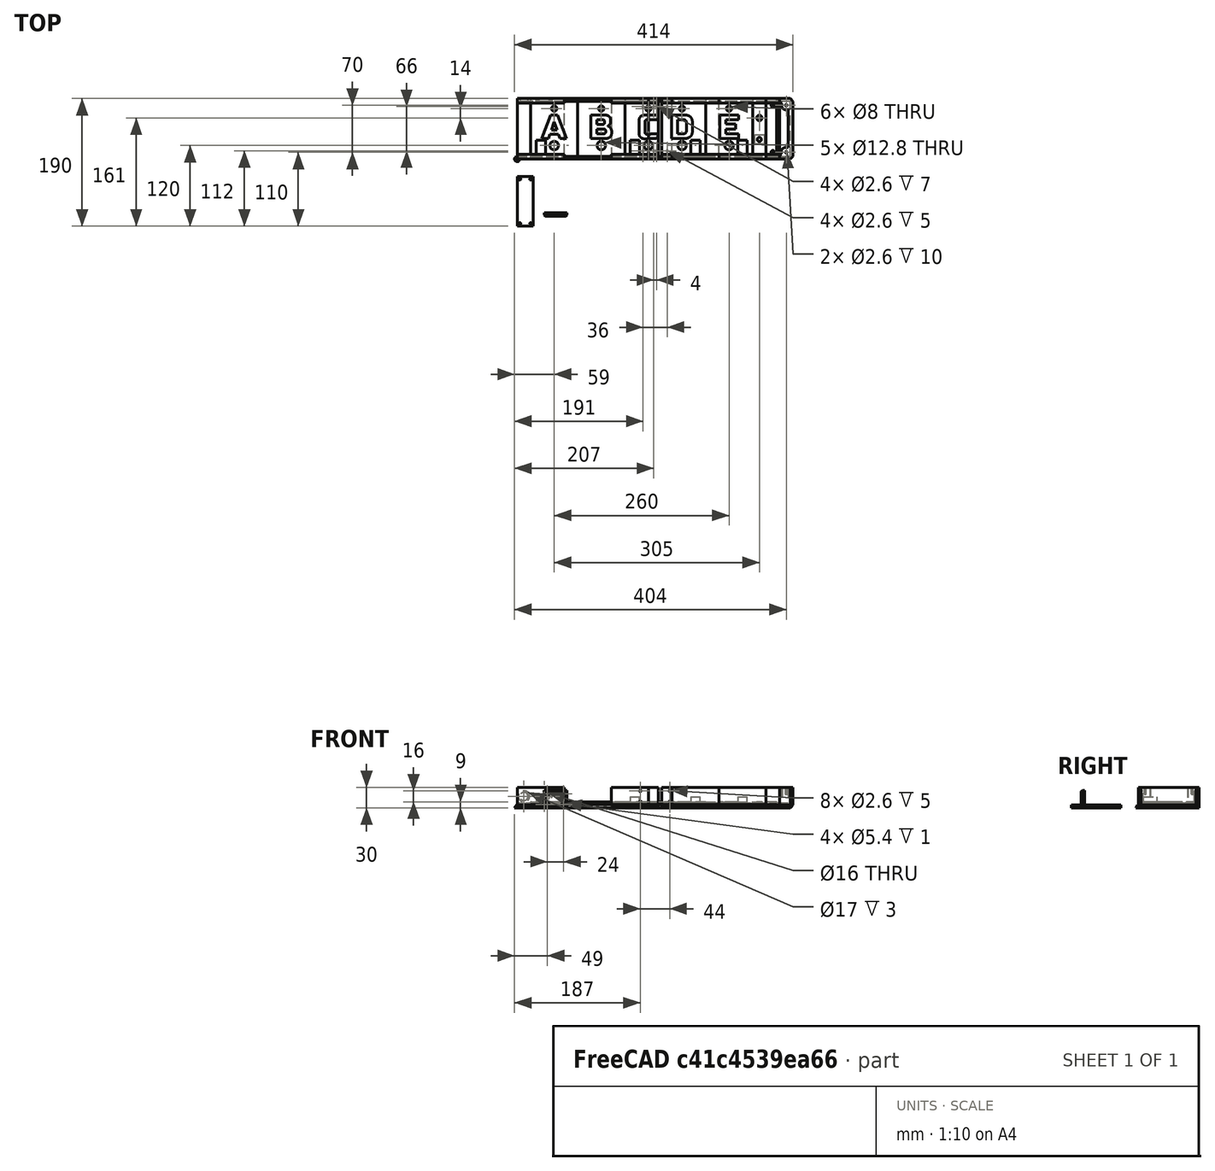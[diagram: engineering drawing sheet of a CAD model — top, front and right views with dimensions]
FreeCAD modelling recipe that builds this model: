
FCSTD DOCUMENT  (FreeCAD 1.0R39319 (Git))
Label: controller
License: All rights reserved
LicenseURL: https://en.wikipedia.org/wiki/All_rights_reserved
objects: Sketcher::SketchObject×34, PartDesign::Body×24, PartDesign::Pocket×17, PartDesign::Pad×15, PartDesign::FeatureBase×15, PartDesign::Chamfer×8, Part::FeaturePython×7, Part::Part2DObjectPython×5, Part::Extrusion×5, Part::Cut×5, App::Part×4, App::Link×4, Part::Plane×2, App::DocumentObjectGroup×2, PartDesign::Plane×1, PartDesign::AdditiveLoft×1, App::FeaturePython×1, Assembly::JointGroup×1, Assembly::AssemblyObject×1
note: 270 computed .brp shape members not serialized (recipe doc carries the construction recipe); baked Part::Feature solids carry a one-line shape summary decoded from their .brp

FEATURE [Sketcher::SketchObject] Sketch
  ArcFitTolerance = 1e-06
  AttachmentSupport = -> [XY_Plane]
  FullyConstrained = true
  MakeInternals = false
  MapMode = 5
  sketch-geometry (4):
    g0: LineSegment StartX=0 StartY=0 StartZ=0 EndX=70 EndY=0 EndZ=0
    g1: LineSegment StartX=70 StartY=0 StartZ=0 EndX=70 EndY=90 EndZ=0
    g2: LineSegment StartX=70 StartY=90 StartZ=0 EndX=0 EndY=90 EndZ=0
    g3: LineSegment StartX=0 StartY=90 StartZ=0 EndX=0 EndY=0 EndZ=0
  constraints (11):
    c: Coincident(g0,g1)
    c: Coincident(g1,g2)
    c: Coincident(g2,g3)
    c: Coincident(g3,g0)
    c: Horizontal(g0)
    c: Horizontal(g2)
    c: Vertical(g1)
    c: Vertical(g3)
    c: Distance(g1,g3) = 70
    c: Distance(g0,g2) = 90
    c: Coincident(g0,g-1)
FEATURE [PartDesign::Pad] Pad
  Direction = (0,0,1)
  Length = 7
  Length2 = 10
  Profile = -> Sketch
  ReferenceAxis = -> Sketch [N_Axis]
  Refine = true
  Suppressed = false
  Type = 0
FEATURE [Sketcher::SketchObject] Sketch001
  ArcFitTolerance = 1e-06
  AttachmentSupport = -> [Pad]
  ExternalGeometry = -> [Pad]
  FullyConstrained = true
  MakeInternals = false
  MapMode = 5
  Placement = pos=(0,0,7) rot=(0,0,1;0rad)
  sketch-geometry (4):
    g0: LineSegment StartX=0 StartY=90 StartZ=0 EndX=0 EndY=83 EndZ=0
    g1: LineSegment StartX=0 StartY=83 StartZ=0 EndX=70 EndY=83 EndZ=0
    g2: LineSegment StartX=70 StartY=83 StartZ=0 EndX=70 EndY=90 EndZ=0
    g3: LineSegment StartX=70 StartY=90 StartZ=0 EndX=0 EndY=90 EndZ=0
  constraints (11):
    c: Coincident(g0,g1)
    c: Coincident(g1,g2)
    c: Coincident(g2,g3)
    c: Coincident(g3,g0)
    c: Vertical(g0)
    c: Vertical(g2)
    c: Horizontal(g1)
    c: Horizontal(g3)
    c: Distance(g0,g2) = 70
    c: Distance(g1,g3) = 7
    c: Coincident(g0,g-3)
FEATURE [PartDesign::Pad] Pad001
  BaseFeature = -> Pad
  Direction = (0,0,1)
  Length = 23
  Length2 = 10
  Profile = -> Sketch001
  ReferenceAxis = -> Sketch001 [N_Axis]
  Refine = true
  Suppressed = false
  Type = 0
FEATURE [Sketcher::SketchObject] Sketch002
  ArcFitTolerance = 1e-06
  AttachmentSupport = -> [Pad001]
  ExternalGeometry = -> [Pad001]
  FullyConstrained = true
  MakeInternals = false
  MapMode = 5
  Placement = pos=(0,0,7) rot=(0,0,1;0rad)
  sketch-geometry (4):
    g0: LineSegment StartX=28 StartY=0 StartZ=0 EndX=42 EndY=0 EndZ=0
    g1: LineSegment StartX=42 StartY=0 StartZ=0 EndX=42 EndY=28 EndZ=0
    g2: LineSegment StartX=42 StartY=28 StartZ=0 EndX=28 EndY=28 EndZ=0
    g3: LineSegment StartX=28 StartY=28 StartZ=0 EndX=28 EndY=0 EndZ=0
  constraints (12):
    c: Coincident(g0,g1)
    c: Coincident(g1,g2)
    c: Coincident(g2,g3)
    c: Coincident(g3,g0)
    c: Horizontal(g0)
    c: Horizontal(g2)
    c: Vertical(g1)
    c: Vertical(g3)
    c: Distance(g1,g3) = 14
    c: Distance(g0,g2) = 28
    c: PointOnObject(g0,g-1)
    c: Distance(g-3,g1) = 28
FEATURE [PartDesign::Pad] Pad002
  BaseFeature = -> Pad001
  Direction = (0,0,1)
  Length = 9
  Length2 = 10
  Profile = -> Sketch002
  ReferenceAxis = -> Sketch002 [N_Axis]
  Refine = true
  Suppressed = false
  Type = 0
FEATURE [Sketcher::SketchObject] Sketch003
  ArcFitTolerance = 1e-06
  AttachmentSupport = -> [Pad002]
  FullyConstrained = true
  MakeInternals = false
  MapMode = 5
  Placement = pos=(0,0,7) rot=(0,0,1;0rad)
  sketch-geometry (4):
    g0: LineSegment StartX=0 StartY=0 StartZ=0 EndX=70 EndY=0 EndZ=0
    g1: LineSegment StartX=70 StartY=0 StartZ=0 EndX=70 EndY=7 EndZ=0
    g2: LineSegment StartX=70 StartY=7 StartZ=0 EndX=0 EndY=7 EndZ=0
    g3: LineSegment StartX=0 StartY=7 StartZ=0 EndX=0 EndY=0 EndZ=0
  constraints (11):
    c: Coincident(g0,g1)
    c: Coincident(g1,g2)
    c: Coincident(g2,g3)
    c: Coincident(g3,g0)
    c: Horizontal(g0)
    c: Horizontal(g2)
    c: Vertical(g1)
    c: Vertical(g3)
    c: Distance(g1,g3) = 70
    c: Distance(g0,g2) = 7
    c: Coincident(g0,g-1)
FEATURE [PartDesign::Pad] Pad003
  BaseFeature = -> Pad002
  Direction = (0,0,1)
  Length = 23
  Length2 = 10
  Profile = -> Sketch003
  ReferenceAxis = -> Sketch003 [N_Axis]
  Refine = true
  Suppressed = false
  Type = 0
FEATURE [Part::Plane] Plane
  AttacherType = Attacher::AttachEngine3D
  Length = 100
  Placement = pos=(195,0,0) rot=(0.58,0.58,0.58;2.0944rad)
  Width = 100
FEATURE [Sketcher::SketchObject] Sketch010
  ArcFitTolerance = 1e-06
  AttachmentSupport = -> [XY_Plane005]
  FullyConstrained = true
  MakeInternals = false
  MapMode = 5
  sketch-geometry (4):
    g0: LineSegment StartX=0 StartY=0 StartZ=0 EndX=20 EndY=0 EndZ=0
    g1: LineSegment StartX=20 StartY=0 StartZ=0 EndX=20 EndY=90 EndZ=0
    g2: LineSegment StartX=20 StartY=90 StartZ=0 EndX=0 EndY=90 EndZ=0
    g3: LineSegment StartX=0 StartY=90 StartZ=0 EndX=0 EndY=0 EndZ=0
  constraints (11):
    c: Coincident(g0,g1)
    c: Coincident(g1,g2)
    c: Coincident(g2,g3)
    c: Coincident(g3,g0)
    c: Horizontal(g0)
    c: Horizontal(g2)
    c: Vertical(g1)
    c: Vertical(g3)
    c: Distance(g1,g3) = 20
    c: Distance(g0,g2) = 90
    c: Coincident(g0,g-1)
FEATURE [PartDesign::Pad] Pad004
  Direction = (0,0,1)
  Length = 7
  Length2 = 10
  Profile = -> Sketch010
  ReferenceAxis = -> Sketch010 [N_Axis]
  Refine = true
  Suppressed = false
  Type = 0
FEATURE [Sketcher::SketchObject] Sketch011
  ArcFitTolerance = 1e-06
  AttachmentSupport = -> [Pad004]
  ExternalGeometry = -> [Pad004]
  FullyConstrained = true
  MakeInternals = false
  MapMode = 5
  Placement = pos=(0,0,7) rot=(0,0,1;0rad)
  sketch-geometry (8):
    g0: LineSegment StartX=20 StartY=90 StartZ=0 EndX=7 EndY=90 EndZ=0
    g1: LineSegment StartX=7 StartY=90 StartZ=0 EndX=7 EndY=83 EndZ=0
    g2: LineSegment StartX=7 StartY=83 StartZ=0 EndX=20 EndY=83 EndZ=0
    g3: LineSegment StartX=20 StartY=83 StartZ=0 EndX=20 EndY=90 EndZ=0
    g4: LineSegment StartX=20 StartY=0 StartZ=0 EndX=20 EndY=7 EndZ=0
    g5: LineSegment StartX=20 StartY=7 StartZ=0 EndX=7 EndY=7 EndZ=0
    g6: LineSegment StartX=7 StartY=7 StartZ=0 EndX=7 EndY=0 EndZ=0
    g7: LineSegment StartX=7 StartY=0 StartZ=0 EndX=20 EndY=0 EndZ=0
  constraints (22):
    c: Coincident(g0,g1)
    c: Coincident(g1,g2)
    c: Coincident(g2,g3)
    c: Coincident(g3,g0)
    c: Horizontal(g0)
    c: Horizontal(g2)
    c: Vertical(g1)
    c: Vertical(g3)
    c: Distance(g1,g3) = 13
    c: Distance(g0,g2) = 7
    c: Coincident(g0,g-4)
    c: Coincident(g4,g5)
    c: Coincident(g5,g6)
    c: Coincident(g6,g7)
    c: Coincident(g7,g4)
    c: Vertical(g4)
    c: Vertical(g6)
    c: Horizontal(g5)
    c: Horizontal(g7)
    c: Distance(g4,g6) = 13
    c: Distance(g5,g7) = 7
    c: Coincident(g4,g-4)
FEATURE [PartDesign::Pad] Pad005
  BaseFeature = -> Pad004
  Direction = (0,0,1)
  Length = 23
  Length2 = 10
  Profile = -> Sketch011
  ReferenceAxis = -> Sketch011 [N_Axis]
  Refine = true
  Suppressed = false
  Type = 0
FEATURE [Sketcher::SketchObject] Sketch012
  ArcFitTolerance = 1e-06
  AttachmentSupport = -> [Pad005]
  FullyConstrained = true
  MakeInternals = false
  MapMode = 5
  Placement = pos=(0,0,7) rot=(0,0,1;0rad)
  sketch-geometry (4):
    g0: LineSegment StartX=0 StartY=0 StartZ=0 EndX=7 EndY=0 EndZ=0
    g1: LineSegment StartX=7 StartY=0 StartZ=0 EndX=7 EndY=90 EndZ=0
    g2: LineSegment StartX=7 StartY=90 StartZ=0 EndX=0 EndY=90 EndZ=0
    g3: LineSegment StartX=0 StartY=90 StartZ=0 EndX=0 EndY=0 EndZ=0
  constraints (11):
    c: Coincident(g0,g1)
    c: Coincident(g1,g2)
    c: Coincident(g2,g3)
    c: Coincident(g3,g0)
    c: Horizontal(g0)
    c: Horizontal(g2)
    c: Vertical(g1)
    c: Vertical(g3)
    c: Distance(g1,g3) = 7
    c: Distance(g0,g2) = 90
    c: Coincident(g0,g-1)
FEATURE [PartDesign::Pad] Pad006
  BaseFeature = -> Pad005
  Direction = (0,0,1)
  Length = 23
  Length2 = 10
  Profile = -> Sketch012
  ReferenceAxis = -> Sketch012 [N_Axis]
  Refine = true
  Suppressed = false
  Type = 0
FEATURE [Sketcher::SketchObject] Sketch013
  ArcFitTolerance = 1e-06
  AttachmentSupport = -> [Pad006]
  ExternalGeometry = -> [Pad006]
  FullyConstrained = true
  MakeInternals = false
  MapMode = 5
  Placement = pos=(0,0,7) rot=(0,0,1;0rad)
  sketch-geometry (2):
    g0: Circle CenterX=10 CenterY=80 CenterZ=0 NormalX=0 NormalY=0 NormalZ=1 AngleXU=0 Radius=7.5
    g1: Circle CenterX=10 CenterY=10 CenterZ=0 NormalX=0 NormalY=0 NormalZ=1 AngleXU=0 Radius=7
  constraints (6):
    c: Diameter(g0) = 15
    c: DistanceY(g0,g-3) = 10
    c: DistanceX(g-3,g0) = 10
    c: Diameter(g1) = 14
    c: DistanceX(g-1,g1) = 10
    c: DistanceY(g-1,g1) = 10
FEATURE [PartDesign::Pad] Pad007
  BaseFeature = -> Pad006
  Direction = (0,0,1)
  Length = 23
  Length2 = 10
  Profile = -> Sketch013
  ReferenceAxis = -> Sketch013 [N_Axis]
  Refine = true
  Suppressed = false
  Type = 0
FEATURE [Sketcher::SketchObject] Sketch014
  ArcFitTolerance = 1e-06
  AttachmentSupport = -> [Pad007]
  ExternalGeometry = -> [Pad007]
  FullyConstrained = true
  MakeInternals = false
  MapMode = 5
  Placement = pos=(0,0,30) rot=(0,0,1;0rad)
  sketch-geometry (2):
    g0: Circle CenterX=10 CenterY=80 CenterZ=0 NormalX=0 NormalY=0 NormalZ=1 AngleXU=0 Radius=1.3
    g1: Circle CenterX=10 CenterY=10 CenterZ=0 NormalX=0 NormalY=0 NormalZ=1 AngleXU=0 Radius=1.3
  constraints (6):
    c: Diameter(g0) = 2.6
    c: Diameter(g1) = 2.6
    c: DistanceY(g0,g-3) = 10
    c: DistanceX(g-3,g0) = 10
    c: DistanceX(g-1,g1) = 10
    c: DistanceY(g-1,g1) = 10
FEATURE [PartDesign::Pocket] Pocket
  BaseFeature = -> Pad007
  Direction = (0,0,-1)
  Length = 10
  Length2 = 5
  Profile = -> Sketch014
  ReferenceAxis = -> Sketch014 [N_Axis]
  Refine = true
  Suppressed = false
  Type = 0
FEATURE [PartDesign::Chamfer] Chamfer
  Angle = 45
  Base = -> Pad003 [Edge1,Edge3]
  BaseFeature = -> Pad003
  ChamferType = 0
  FlipDirection = false
  Refine = true
  Size = 4
  Size2 = 1
  SupportTransform = false
  Suppressed = false
  UseAllEdges = false
FEATURE [PartDesign::Body] Body  label="base-module"
  AllowCompound = false
  Group = -> [Sketch,Pad,Sketch001,Pad001,Sketch002,Pad002,Sketch003,Pad003,Chamfer]
  Origin = -> Origin
  Placement = pos=(70,0,0) rot=(0,0,1;0rad)
  Tip = -> Chamfer
FEATURE [PartDesign::FeatureBase] Clone
  BaseFeature = -> Body
  Suppressed = false
FEATURE [PartDesign::FeatureBase] Clone001
  BaseFeature = -> Body
  Placement = pos=(70,0,0) rot=(0,0,1;0rad)
  Suppressed = false
FEATURE [PartDesign::Body] Body002  label="split-base-module"
  AllowCompound = false
  Group = -> [Clone001]
  Origin = -> Origin002
  Placement = pos=(70,0,0) rot=(0,0,1;0rad)
  Tip = -> Clone001
FEATURE [Part::FeaturePython] Slice  # WARN: FeaturePython — macro-defined, semantics opaque (R4)
  Base = -> Body002
  Mode = 1
  Tolerance = 0
  Tools = -> [Plane]
FEATURE [PartDesign::FeatureBase] Clone002
  BaseFeature = -> Body
  Placement = pos=(70,0,0) rot=(0,0,1;0rad)
  Suppressed = false
FEATURE [PartDesign::Body] Body003  label="base-module-clone"
  AllowCompound = false
  Group = -> [Clone002]
  Origin = -> Origin003
  Placement = pos=(160,0,0) rot=(0,0,1;0rad)
  Tip = -> Clone002
FEATURE [PartDesign::FeatureBase] Clone003
  BaseFeature = -> Body
  Placement = pos=(70,0,0) rot=(0,0,1;0rad)
  Suppressed = false
FEATURE [PartDesign::Body] Body004  label="base-module-clone001"
  AllowCompound = false
  Group = -> [Clone003]
  Origin = -> Origin004
  Placement = pos=(230,0,0) rot=(0,0,1;0rad)
  Tip = -> Clone003
FEATURE [PartDesign::Chamfer] Chamfer001
  Angle = 45
  Base = -> Pocket [Edge3,Edge4,Edge1]
  BaseFeature = -> Pocket
  ChamferType = 0
  FlipDirection = false
  Refine = true
  Size = 4
  Size2 = 1
  SupportTransform = false
  Suppressed = false
  UseAllEdges = false
FEATURE [PartDesign::FeatureBase] Clone004
  BaseFeature = -> Body
  Placement = pos=(70,0,0) rot=(0,0,1;0rad)
  Suppressed = false
FEATURE [Part::Plane] Plane001
  AttacherType = Attacher::AttachEngine3D
  Length = 200
  Placement = pos=(195,0,0) rot=(0.57735,0.57735,0.57735;2.0944rad)
  Width = 200
FEATURE [Sketcher::SketchObject] Sketch015
  ArcFitTolerance = 1e-06
  AttachmentSupport = -> [Clone004]
  ExternalGeometry = -> [Clone004]
  FullyConstrained = true
  MakeInternals = false
  MapMode = 5
  Placement = pos=(70,0,0) rot=(1,0,0;1.5708rad)
  sketch-geometry (4):
    g0: Circle CenterX=43 CenterY=25 CenterZ=0 NormalX=0 NormalY=0 NormalZ=1 AngleXU=0 Radius=1.3
    g1: Circle CenterX=43 CenterY=9 CenterZ=0 NormalX=0 NormalY=0 NormalZ=1 AngleXU=0 Radius=1.3
    g2: Circle CenterX=67 CenterY=25 CenterZ=0 NormalX=0 NormalY=0 NormalZ=1 AngleXU=0 Radius=1.3
    g3: Circle CenterX=67 CenterY=9 CenterZ=0 NormalX=0 NormalY=0 NormalZ=1 AngleXU=0 Radius=1.3
  constraints (12):
    c: Diameter(g0) = 2.6
    c: Diameter(g1) = 2.6
    c: Diameter(g2) = 2.6
    c: Diameter(g3) = 2.6
    c: Distance(g0,g-3) = 5
    c: Distance(g2,g-3) = 5
    c: Distance(g1,g-5) = 5
    c: Distance(g3,g-5) = 5
    c: Distance(g2,g-4) = 3
    c: Distance(g3,g-4) = 3
    c: Distance(g1,g-2) = 43
    c: Distance(g0,g-2) = 43
FEATURE [PartDesign::Pocket] Pocket001
  BaseFeature = -> Clone004
  Direction = (0,1,-2e-16)
  Length = 5
  Length2 = 5
  Placement = pos=(70,0,0) rot=(0,0,1;0rad)
  Profile = -> Sketch015
  ReferenceAxis = -> Sketch015 [N_Axis]
  Refine = true
  Suppressed = false
  Type = 0
FEATURE [Sketcher::SketchObject] Sketch016
  ArcFitTolerance = 1e-06
  AttachmentSupport = -> [Pocket001]
  ExternalGeometry = -> [Pocket001]
  FullyConstrained = true
  MakeInternals = false
  MapMode = 5
  Placement = pos=(70,90,0) rot=(0,0.707107,0.707107;3.14159rad)
  sketch-geometry (4):
    g0: Circle CenterX=-43 CenterY=25 CenterZ=0 NormalX=0 NormalY=0 NormalZ=1 AngleXU=0 Radius=1.3
    g1: Circle CenterX=-43 CenterY=9 CenterZ=0 NormalX=0 NormalY=0 NormalZ=1 AngleXU=0 Radius=1.3
    g2: Circle CenterX=-67 CenterY=25 CenterZ=0 NormalX=0 NormalY=0 NormalZ=1 AngleXU=0 Radius=1.3
    g3: Circle CenterX=-67 CenterY=9 CenterZ=0 NormalX=0 NormalY=0 NormalZ=1 AngleXU=0 Radius=1.3
  constraints (12):
    c: Diameter(g0) = 2.6
    c: Diameter(g1) = 2.6
    c: Diameter(g2) = 2.6
    c: Diameter(g3) = 2.6
    c: Distance(g2,g-3) = 5
    c: Distance(g3,g-5) = 5
    c: Distance(g3,g-4) = 3
    c: Distance(g2,g-4) = 3
    c: Distance(g0,g-3) = 5
    c: Distance(g1,g-5) = 5
    c: Distance(g1,g-2) = 43
    c: Distance(g0,g-2) = 43
FEATURE [PartDesign::Pocket] Pocket002
  BaseFeature = -> Pocket001
  Direction = (0,-1,2e-16)
  Length = 5
  Length2 = 5
  Placement = pos=(70,0,0) rot=(0,0,1;0rad)
  Profile = -> Sketch016
  ReferenceAxis = -> Sketch016 [N_Axis]
  Refine = true
  Suppressed = false
  Type = 0
FEATURE [Sketcher::SketchObject] Sketch017
  ArcFitTolerance = 1e-06
  AttachmentSupport = -> [Pocket002]
  ExternalGeometry = -> [Pocket002]
  FullyConstrained = true
  MakeInternals = false
  MapMode = 5
  Placement = pos=(70,0,7) rot=(0,0,1;0rad)
  sketch-geometry (4):
    g0: Circle CenterX=47 CenterY=78 CenterZ=0 NormalX=0 NormalY=0 NormalZ=1 AngleXU=0 Radius=1.3
    g1: Circle CenterX=47 CenterY=12 CenterZ=0 NormalX=0 NormalY=0 NormalZ=1 AngleXU=0 Radius=1.3
    g2: Circle CenterX=63 CenterY=78 CenterZ=0 NormalX=0 NormalY=0 NormalZ=1 AngleXU=0 Radius=1.3
    g3: Circle CenterX=63 CenterY=12 CenterZ=0 NormalX=0 NormalY=0 NormalZ=1 AngleXU=0 Radius=1.3
  constraints (12):
    c: Diameter(g0) = 2.6
    c: Diameter(g1) = 2.6
    c: Diameter(g2) = 2.6
    c: Diameter(g3) = 2.6
    c: Distance(g0,g-2) = 47
    c: Distance(g1,g-2) = 47
    c: DistanceY(g-5,g1) = 5
    c: DistanceY(g0,g-5) = 5
    c: DistanceX(g2,g-5) = 7
    c: DistanceY(g2,g-5) = 5
    c: DistanceY(g-5,g3) = 5
    c: DistanceX(g3,g-5) = 7
FEATURE [PartDesign::Pocket] Pocket003
  BaseFeature = -> Pocket002
  Direction = (0,0,-1)
  Length = 5
  Length2 = 5
  Placement = pos=(70,0,0) rot=(0,0,1;0rad)
  Profile = -> Sketch017
  ReferenceAxis = -> Sketch017 [N_Axis]
  Refine = true
  Suppressed = false
  Type = 0
FEATURE [PartDesign::Body] Body006  label="split-module"
  AllowCompound = false
  Group = -> [Clone004,Sketch015,Pocket001,Sketch016,Pocket002,Sketch017,Pocket003]
  Origin = -> Origin006
  Placement = pos=(70,0,0) rot=(0,0,1;0rad)
  Tip = -> Pocket003
FEATURE [Part::FeaturePython] Slice001  # WARN: FeaturePython — macro-defined, semantics opaque (R4)
  Base = -> Body006
  Mode = 1
  Tolerance = 0
  Tools = -> [Plane001]
FEATURE [PartDesign::Chamfer] Chamfer002
  Angle = 45
  Base = -> Chamfer001 [Edge19,Edge40]
  BaseFeature = -> Chamfer001
  ChamferType = 0
  FlipDirection = false
  Refine = true
  Size = 4
  Size2 = 1
  SupportTransform = false
  Suppressed = false
  UseAllEdges = false
FEATURE [PartDesign::Body] Body005  label="left-side"
  AllowCompound = false
  Group = -> [Sketch010,Pad004,Sketch011,Pad005,Sketch012,Pad006,Sketch013,Pad007,Sketch014,Pocket,Chamfer001,Chamfer002]
  Origin = -> Origin005
  Placement = pos=(-20,0,0) rot=(0,0,1;0rad)
  Tip = -> Chamfer002
FEATURE [PartDesign::FeatureBase] Clone005
  BaseFeature = -> Body005
  Placement = pos=(-20,0,0) rot=(0,0,1;0rad)
  Suppressed = false
FEATURE [PartDesign::Body] Body007  label="right-side"
  AllowCompound = false
  Group = -> [Clone005]
  Origin = -> Origin007
  Placement = pos=(390,90,0) rot=(0,0,1;3.14159rad)
  Tip = -> Clone005
FEATURE [Sketcher::SketchObject] Sketch018
  ArcFitTolerance = 1e-06
  AttachmentSupport = -> [XY_Plane008]
  FullyConstrained = true
  MakeInternals = false
  MapMode = 5
  sketch-geometry (4):
    g0: LineSegment StartX=0 StartY=9e-16 StartZ=0 EndX=20 EndY=9e-16 EndZ=0
    g1: LineSegment StartX=20 StartY=9e-16 StartZ=0 EndX=20 EndY=90 EndZ=0
    g2: LineSegment StartX=20 StartY=90 StartZ=0 EndX=0 EndY=90 EndZ=0
    g3: LineSegment StartX=0 StartY=90 StartZ=0 EndX=0 EndY=0 EndZ=0
  constraints (11):
    c: Coincident(g0,g1)
    c: Coincident(g1,g2)
    c: Coincident(g2,g3)
    c: Coincident(g3,g0)
    c: Horizontal(g0)
    c: Horizontal(g2)
    c: Vertical(g1)
    c: Vertical(g3)
    c: Distance(g1,g3) = 20
    c: Distance(g0,g2) = 90
    c: Coincident(g0,g-1)
FEATURE [PartDesign::Pad] Pad008
  Direction = (0,0,1)
  Length = 7
  Length2 = 10
  Profile = -> Sketch018
  ReferenceAxis = -> Sketch018 [N_Axis]
  Refine = true
  Suppressed = false
  Type = 0
FEATURE [Sketcher::SketchObject] Sketch019
  ArcFitTolerance = 1e-06
  AttachmentSupport = -> [Pad008]
  ExternalGeometry = -> [Pad008]
  FullyConstrained = true
  MakeInternals = false
  MapMode = 5
  Placement = pos=(0,0,7) rot=(0,0,1;0rad)
  sketch-geometry (8):
    g0: LineSegment StartX=20 StartY=90 StartZ=0 EndX=0 EndY=90 EndZ=0
    g1: LineSegment StartX=0 StartY=90 StartZ=0 EndX=0 EndY=83 EndZ=0
    g2: LineSegment StartX=0 StartY=83 StartZ=0 EndX=20 EndY=83 EndZ=0
    g3: LineSegment StartX=20 StartY=83 StartZ=0 EndX=20 EndY=90 EndZ=0
    g4: LineSegment StartX=0 StartY=0 StartZ=0 EndX=20 EndY=0 EndZ=0
    g5: LineSegment StartX=20 StartY=0 StartZ=0 EndX=20 EndY=7 EndZ=0
    g6: LineSegment StartX=20 StartY=7 StartZ=0 EndX=0 EndY=7 EndZ=0
    g7: LineSegment StartX=0 StartY=7 StartZ=0 EndX=0 EndY=0 EndZ=0
  constraints (22):
    c: Coincident(g0,g1)
    c: Coincident(g1,g2)
    c: Coincident(g2,g3)
    c: Coincident(g3,g0)
    c: Horizontal(g0)
    c: Horizontal(g2)
    c: Vertical(g1)
    c: Vertical(g3)
    c: Distance(g1,g3) = 20
    c: Distance(g0,g2) = 7
    c: Coincident(g0,g-3)
    c: Coincident(g4,g5)
    c: Coincident(g5,g6)
    c: Coincident(g6,g7)
    c: Coincident(g7,g4)
    c: Horizontal(g4)
    c: Horizontal(g6)
    c: Vertical(g5)
    c: Vertical(g7)
    c: Distance(g5,g7) = 20
    c: Distance(g4,g6) = 7
    c: Coincident(g4,g-1)
FEATURE [PartDesign::Pad] Pad009
  BaseFeature = -> Pad008
  Direction = (0,0,1)
  Length = 23
  Length2 = 10
  Profile = -> Sketch019
  ReferenceAxis = -> Sketch019 [N_Axis]
  Refine = true
  Suppressed = false
  Type = 0
FEATURE [PartDesign::Chamfer] Chamfer003
  Angle = 45
  Base = -> Pad009 [Edge1,Edge3]
  BaseFeature = -> Pad009
  ChamferType = 0
  FlipDirection = false
  Refine = true
  Size = 4
  Size2 = 1
  SupportTransform = false
  Suppressed = false
  UseAllEdges = false
FEATURE [PartDesign::Body] Body008  label="20mm extension"
  AllowCompound = false
  Group = -> [Sketch018,Pad008,Sketch019,Pad009,Chamfer003]
  Origin = -> Origin008
  Placement = pos=(370,0,0) rot=(0,0,1;0rad)
  Tip = -> Chamfer003
FEATURE [Sketcher::SketchObject] Sketch020
  ArcFitTolerance = 1e-06
  AttachmentSupport = -> [XY_Plane009]
  FullyConstrained = true
  MakeInternals = false
  MapMode = 5
  sketch-geometry (4):
    g0: LineSegment StartX=0 StartY=0 StartZ=0 EndX=24 EndY=0 EndZ=0
    g1: LineSegment StartX=24 StartY=0 StartZ=0 EndX=24 EndY=74 EndZ=0
    g2: LineSegment StartX=24 StartY=74 StartZ=0 EndX=0 EndY=74 EndZ=0
    g3: LineSegment StartX=0 StartY=74 StartZ=0 EndX=0 EndY=0 EndZ=0
  constraints (11):
    c: Coincident(g0,g1)
    c: Coincident(g1,g2)
    c: Coincident(g2,g3)
    c: Coincident(g3,g0)
    c: Horizontal(g0)
    c: Horizontal(g2)
    c: Vertical(g1)
    c: Vertical(g3)
    c: Distance(g1,g3) = 24
    c: Distance(g0,g2) = 74
    c: Coincident(g0,g-1)
FEATURE [PartDesign::Pad] Pad010
  Direction = (0,0,1)
  Length = 4
  Length2 = 10
  Profile = -> Sketch020
  ReferenceAxis = -> Sketch020 [N_Axis]
  Refine = true
  Suppressed = false
  Type = 0
FEATURE [Sketcher::SketchObject] Sketch021
  ArcFitTolerance = 1e-06
  AttachmentSupport = -> [Pad010]
  ExternalGeometry = -> [Pad010]
  FullyConstrained = true
  MakeInternals = false
  MapMode = 5
  Placement = pos=(0,0,4) rot=(0,0,1;0rad)
  sketch-geometry (4):
    g0: Circle CenterX=20 CenterY=70 CenterZ=0 NormalX=0 NormalY=0 NormalZ=1 AngleXU=0 Radius=1.3
    g1: Circle CenterX=4 CenterY=70 CenterZ=0 NormalX=0 NormalY=0 NormalZ=1 AngleXU=0 Radius=1.3
    g2: Circle CenterX=4 CenterY=4 CenterZ=0 NormalX=0 NormalY=0 NormalZ=1 AngleXU=0 Radius=1.3
    g3: Circle CenterX=20 CenterY=4 CenterZ=0 NormalX=0 NormalY=0 NormalZ=1 AngleXU=0 Radius=1.3
  constraints (12):
    c: Diameter(g0) = 2.6
    c: DistanceX(g0,g-3) = 4
    c: DistanceY(g0,g-3) = 4
    c: Diameter(g1) = 2.6
    c: Diameter(g2) = 2.6
    c: Diameter(g3) = 2.6
    c: DistanceY(g1,g-3) = 4
    c: DistanceX(g1,g0) = 16
    c: DistanceX(g3,g-3) = 4
    c: DistanceY(g-3,g3) = 4
    c: DistanceY(g3,g2) = 0
    c: DistanceX(g2,g1) = 0
FEATURE [PartDesign::Pocket] Pocket004
  BaseFeature = -> Pad010
  Direction = (0,0,-1)
  Length = 5
  Length2 = 5
  Profile = -> Sketch021
  ReferenceAxis = -> Sketch021 [N_Axis]
  Refine = true
  Suppressed = false
  Type = 0
FEATURE [PartDesign::Body] Body009  label="lid-and-base-splint"
  AllowCompound = false
  Group = -> [Sketch020,Pad010,Sketch021,Pocket004]
  Origin = -> Origin009
  Placement = pos=(0,-100,0) rot=(0,0,1;0rad)
  Tip = -> Pocket004
FEATURE [Sketcher::SketchObject] Sketch022
  ArcFitTolerance = 1e-06
  AttachmentSupport = -> [XZ_Plane010]
  FullyConstrained = true
  MakeInternals = false
  MapMode = 5
  Placement = pos=(0,0,0) rot=(1,0,0;1.5708rad)
  sketch-geometry (4):
    g0: LineSegment StartX=0 StartY=0 StartZ=0 EndX=34 EndY=0 EndZ=0
    g1: LineSegment StartX=34 StartY=0 StartZ=0 EndX=34 EndY=26 EndZ=0
    g2: LineSegment StartX=34 StartY=26 StartZ=0 EndX=0 EndY=26 EndZ=0
    g3: LineSegment StartX=0 StartY=26 StartZ=0 EndX=0 EndY=0 EndZ=0
  constraints (11):
    c: Coincident(g0,g1)
    c: Coincident(g1,g2)
    c: Coincident(g2,g3)
    c: Coincident(g3,g0)
    c: Horizontal(g0)
    c: Horizontal(g2)
    c: Vertical(g1)
    c: Vertical(g3)
    c: Distance(g1,g3) = 34
    c: Distance(g0,g2) = 26
    c: Coincident(g0,g-1)
FEATURE [PartDesign::Pad] Pad011
  Direction = (0,-1,2e-16)
  Length = 5
  Length2 = 10
  Placement = pos=(0,0,0) rot=(1,0,0;1.5708rad)
  Profile = -> Sketch022
  ReferenceAxis = -> Sketch022 [N_Axis]
  Refine = true
  Suppressed = false
  Type = 0
FEATURE [Sketcher::SketchObject] Sketch023
  ArcFitTolerance = 1e-06
  AttachmentSupport = -> [Pad011]
  ExternalGeometry = -> [Pad011]
  FullyConstrained = true
  MakeInternals = false
  MapMode = 5
  Placement = pos=(0,-5,0) rot=(1,0,0;1.5708rad)
  sketch-geometry (4):
    g0: Circle CenterX=5 CenterY=21 CenterZ=0 NormalX=0 NormalY=0 NormalZ=1 AngleXU=0 Radius=1.3
    g1: Circle CenterX=29 CenterY=21 CenterZ=0 NormalX=0 NormalY=0 NormalZ=1 AngleXU=0 Radius=1.3
    g2: Circle CenterX=5 CenterY=5 CenterZ=0 NormalX=0 NormalY=0 NormalZ=1 AngleXU=0 Radius=1.3
    g3: Circle CenterX=29 CenterY=5 CenterZ=0 NormalX=0 NormalY=0 NormalZ=1 AngleXU=0 Radius=1.3
  constraints (12):
    c: Diameter(g0) = 2.6
    c: Diameter(g1) = 2.6
    c: Diameter(g2) = 2.6
    c: Diameter(g3) = 2.6
    c: Distance(g0,g-3) = 5
    c: Distance(g0,g-2) = 5
    c: Distance(g3,g-4) = 5
    c: Distance(g3,g-1) = 5
    c: Distance(g2,g-2) = 5
    c: Distance(g2,g-1) = 5
    c: Distance(g1,g-3) = 5
    c: Distance(g1,g-4) = 5
FEATURE [PartDesign::Pocket] Pocket005
  BaseFeature = -> Pad011
  Direction = (0,1,-2e-16)
  Length = 5
  Length2 = 5
  Placement = pos=(0,0,0) rot=(1,0,0;1.5708rad)
  Profile = -> Sketch023
  ReferenceAxis = -> Sketch023 [N_Axis]
  Refine = true
  Suppressed = false
  Type = 0
FEATURE [Sketcher::SketchObject] Sketch024
  ArcFitTolerance = 1e-06
  AttachmentSupport = -> [Pocket005]
  ExternalGeometry = -> [Pocket005]
  FullyConstrained = true
  MakeInternals = false
  MapMode = 5
  Placement = pos=(0,-5,0) rot=(1,0,0;1.5708rad)
  sketch-geometry (4):
    g0: Circle CenterX=5 CenterY=21 CenterZ=0 NormalX=0 NormalY=0 NormalZ=1 AngleXU=0 Radius=2.7
    g1: Circle CenterX=29 CenterY=21 CenterZ=0 NormalX=0 NormalY=0 NormalZ=1 AngleXU=0 Radius=2.7
    g2: Circle CenterX=5 CenterY=5 CenterZ=0 NormalX=0 NormalY=0 NormalZ=1 AngleXU=0 Radius=2.7
    g3: Circle CenterX=29 CenterY=5 CenterZ=0 NormalX=0 NormalY=0 NormalZ=1 AngleXU=0 Radius=2.7
  constraints (12):
    c: Diameter(g0) = 5.4
    c: Diameter(g1) = 5.4
    c: Diameter(g2) = 5.4
    c: Diameter(g3) = 5.4
    c: Distance(g0,g-3) = 5
    c: DistanceY(g1,g-4) = 5
    c: DistanceY(g-4,g3) = 5
    c: DistanceY(g-1,g2) = 5
    c: DistanceX(g3,g-4) = 5
    c: DistanceX(g-1,g2) = 5
    c: DistanceX(g-3,g0) = 5
    c: DistanceX(g1,g-4) = 5
FEATURE [PartDesign::Pocket] Pocket006
  BaseFeature = -> Pocket005
  Direction = (0,1,-2e-16)
  Length = 1
  Length2 = 5
  Placement = pos=(0,0,0) rot=(1,0,0;1.5708rad)
  Profile = -> Sketch024
  ReferenceAxis = -> Sketch024 [N_Axis]
  Refine = true
  Suppressed = false
  Type = 0
FEATURE [PartDesign::Chamfer] Chamfer004
  Angle = 45
  Base = -> Pocket006 [Edge7,Edge16,Edge10,Edge4]
  BaseFeature = -> Pocket006
  ChamferType = 0
  FlipDirection = false
  Placement = pos=(0,0,0) rot=(1,0,0;1.5708rad)
  Refine = true
  Size = 1.5
  Size2 = 1
  SupportTransform = false
  Suppressed = false
  UseAllEdges = false
FEATURE [PartDesign::Body] Body010  label="side-splint"
  AllowCompound = false
  Group = -> [Sketch022,Pad011,Sketch023,Pocket005,Sketch024,Pocket006,Chamfer004]
  Origin = -> Origin010
  Placement = pos=(40,-80,0) rot=(0,0,1;0rad)
  Tip = -> Chamfer004
FEATURE [Part::FeaturePython] Slice001_child0  label="Slice001.0"  # WARN: FeaturePython — macro-defined, semantics opaque (R4)
  Base = -> Slice001
  FilterType = 1
  Invert = false
  OverrideMaxVal = 0
  Placement = pos=(20,0,0) rot=(0,0,1;0rad)
  WindowFrom = 80
  WindowTo = 100
  items = 0
FEATURE [Part::FeaturePython] Slice001_child1  label="Slice001.1"  # WARN: FeaturePython — macro-defined, semantics opaque (R4)
  Base = -> Slice001
  FilterType = 1
  Invert = false
  OverrideMaxVal = 0
  WindowFrom = 80
  WindowTo = 100
  items = 1
FEATURE [App::DocumentObjectGroup] GrExplode_Slice001  label="Exploded Slice001"
  Group = -> [Slice001_child1,Slice001_child0]
FEATURE [PartDesign::FeatureBase] BaseFeature
  BaseFeature = -> Slice001_child1
  Suppressed = false
FEATURE [PartDesign::Body] Body011  label="left-split"
  AllowCompound = false
  BaseFeature = -> Slice001_child1
  Group = -> [BaseFeature]
  Origin = -> Origin013
  Tip = -> BaseFeature
FEATURE [PartDesign::FeatureBase] BaseFeature001
  BaseFeature = -> Slice001_child0
  Suppressed = false
FEATURE [PartDesign::Body] Body012  label="right-split"
  AllowCompound = false
  BaseFeature = -> Slice001_child0
  Group = -> [BaseFeature001]
  Origin = -> Origin014
  Placement = pos=(20,0,0) rot=(0,0,1;0rad)
  Tip = -> BaseFeature001
FEATURE [App::Part] Part001  label="right-base"
  Group = -> [Slice001_child0,Slice001_child1,Body006,Slice001,Plane001,Body012,Body003,Body004,Body008,Body007]
  Origin = -> Origin012
  Placement = pos=(-20,0,0) rot=(0,0,1;0rad)
FEATURE [Sketcher::SketchObject] Sketch025
  ArcFitTolerance = 1e-06
  AttachmentSupport = -> [XY_Plane016]
  FullyConstrained = true
  MakeInternals = false
  MapMode = 5
  sketch-geometry (4):
    g0: LineSegment StartX=0 StartY=0 StartZ=0 EndX=70 EndY=0 EndZ=0
    g1: LineSegment StartX=70 StartY=0 StartZ=0 EndX=70 EndY=90 EndZ=0
    g2: LineSegment StartX=70 StartY=90 StartZ=0 EndX=0 EndY=90 EndZ=0
    g3: LineSegment StartX=0 StartY=90 StartZ=0 EndX=0 EndY=0 EndZ=0
  constraints (11):
    c: Coincident(g0,g1)
    c: Coincident(g1,g2)
    c: Coincident(g2,g3)
    c: Coincident(g3,g0)
    c: Horizontal(g0)
    c: Horizontal(g2)
    c: Vertical(g1)
    c: Vertical(g3)
    c: Distance(g1,g3) = 70
    c: Distance(g0,g2) = 90
    c: Coincident(g0,g-1)
FEATURE [PartDesign::Pad] Pad012
  Direction = (0,0,1)
  Length = 9
  Length2 = 10
  Profile = -> Sketch025
  ReferenceAxis = -> Sketch025 [N_Axis]
  Refine = true
  Suppressed = false
  Type = 0
FEATURE [PartDesign::Chamfer] Chamfer005
  Angle = 45
  Base = -> Pad012 [Edge4,Edge10]
  BaseFeature = -> Pad012
  ChamferType = 0
  FlipDirection = false
  Refine = true
  Size = 4
  Size2 = 1
  SupportTransform = false
  Suppressed = false
  UseAllEdges = false
FEATURE [Sketcher::SketchObject] Sketch026
  ArcFitTolerance = 1e-06
  AttachmentSupport = -> [Chamfer005]
  FullyConstrained = true
  MakeInternals = false
  MapMode = 5
  Placement = pos=(0,0,9) rot=(0,0,1;0rad)
  sketch-geometry (2):
    g0: Circle CenterX=35 CenterY=20 CenterZ=0 NormalX=0 NormalY=0 NormalZ=1 AngleXU=0 Radius=6.4
    g1: Circle CenterX=35 CenterY=75 CenterZ=0 NormalX=0 NormalY=0 NormalZ=1 AngleXU=0 Radius=4
  constraints (6):
    c: Diameter(g0) = 12.8
    c: DistanceX(g-1,g0) = 35
    c: DistanceY(g-1,g0) = 20
    c: Diameter(g1) = 8
    c: DistanceX(g-1,g1) = 35
    c: DistanceY(g-1,g1) = 75
FEATURE [PartDesign::Pocket] Pocket007
  BaseFeature = -> Chamfer005
  Direction = (0,0,-1)
  Length = 10
  Length2 = 5
  Profile = -> Sketch026
  ReferenceAxis = -> Sketch026 [N_Axis]
  Refine = true
  Suppressed = false
  Type = 0
FEATURE [PartDesign::Body] Body013  label="lid-module"
  AllowCompound = false
  Group = -> [Sketch025,Pad012,Chamfer005,Sketch026,Pocket007]
  Origin = -> Origin016
  Placement = pos=(20,0,0) rot=(0,0,1;0rad)
  Tip = -> Pocket007
FEATURE [PartDesign::FeatureBase] Clone006
  BaseFeature = -> Body013
  Suppressed = false
FEATURE [PartDesign::Body] Body014  label="lid-module-clone"
  AllowCompound = false
  Group = -> [Clone006]
  Origin = -> Origin017
  Placement = pos=(90,0,0) rot=(0,0,1;0rad)
  Tip = -> Clone006
FEATURE [Sketcher::SketchObject] Sketch027
  ArcFitTolerance = 1e-06
  AttachmentSupport = -> [XY_Plane018]
  FullyConstrained = true
  MakeInternals = false
  MapMode = 5
  sketch-geometry (4):
    g0: LineSegment StartX=0 StartY=0 StartZ=0 EndX=20 EndY=0 EndZ=0
    g1: LineSegment StartX=20 StartY=0 StartZ=0 EndX=20 EndY=90 EndZ=0
    g2: LineSegment StartX=20 StartY=90 StartZ=0 EndX=0 EndY=90 EndZ=0
    g3: LineSegment StartX=0 StartY=90 StartZ=0 EndX=0 EndY=0 EndZ=0
  constraints (11):
    c: Coincident(g0,g1)
    c: Coincident(g1,g2)
    c: Coincident(g2,g3)
    c: Coincident(g3,g0)
    c: Horizontal(g0)
    c: Horizontal(g2)
    c: Vertical(g1)
    c: Vertical(g3)
    c: Distance(g1,g3) = 20
    c: Distance(g0,g2) = 90
    c: Coincident(g0,g-1)
FEATURE [PartDesign::Pad] Pad013
  Direction = (0,0,1)
  Length = 9
  Length2 = 10
  Profile = -> Sketch027
  ReferenceAxis = -> Sketch027 [N_Axis]
  Refine = true
  Suppressed = false
  Type = 0
FEATURE [Sketcher::SketchObject] Sketch028
  ArcFitTolerance = 1e-06
  FullyConstrained = true
  MakeInternals = false
  MapMode = 5
  Placement = pos=(0,0,9) rot=(0,0,1;0rad)
  sketch-geometry (2):
    g0: Circle CenterX=10 CenterY=80 CenterZ=0 NormalX=0 NormalY=0 NormalZ=1 AngleXU=0 Radius=2.7
    g1: Circle CenterX=10 CenterY=10 CenterZ=0 NormalX=0 NormalY=0 NormalZ=1 AngleXU=0 Radius=2.7
  constraints (6):
    c: Diameter(g0) = 5.4
    c: Diameter(g1) = 5.4
    c: DistanceX(g-3,g0) = 10
    c: DistanceX(g-1,g1) = 10
    c: DistanceY(g-1,g1) = 10
    c: DistanceY(g0,g-3) = 10
FEATURE [PartDesign::Pocket] Pocket008
  BaseFeature = -> Pad013
  Direction = (0,0,-1)
  Length = 1
  Length2 = 5
  Profile = -> Sketch028
  ReferenceAxis = -> Sketch028 [N_Axis]
  Refine = true
  Suppressed = false
  Type = 0
FEATURE [Sketcher::SketchObject] Sketch029
  ArcFitTolerance = 1e-06
  AttachmentSupport = -> [Pocket008]
  ExternalGeometry = -> [Pocket008]
  FullyConstrained = true
  MakeInternals = false
  MapMode = 5
  Placement = pos=(0,0,9) rot=(0,0,1;0rad)
  sketch-geometry (2):
    g0: Circle CenterX=10 CenterY=80 CenterZ=0 NormalX=0 NormalY=0 NormalZ=1 AngleXU=0 Radius=1.3
    g1: Circle CenterX=10 CenterY=10 CenterZ=0 NormalX=0 NormalY=0 NormalZ=1 AngleXU=0 Radius=1.3
  constraints (6):
    c: Diameter(g0) = 2.6
    c: Diameter(g1) = 2.6
    c: DistanceY(g-1,g1) = 10
    c: DistanceX(g-1,g1) = 10
    c: DistanceY(g0,g-3) = 10
    c: DistanceX(g-3,g0) = 10
FEATURE [PartDesign::Pocket] Pocket009
  BaseFeature = -> Pocket008
  Direction = (0,0,-1)
  Length = 10
  Length2 = 5
  Profile = -> Sketch029
  ReferenceAxis = -> Sketch029 [N_Axis]
  Refine = true
  Suppressed = false
  Type = 0
FEATURE [PartDesign::Chamfer] Chamfer006
  Angle = 45
  Base = -> Pocket009 [Edge5,Edge1,Edge4,Edge7,Edge14]
  BaseFeature = -> Pocket009
  ChamferType = 0
  FlipDirection = false
  Refine = true
  Size = 4
  Size2 = 1
  SupportTransform = false
  Suppressed = false
  UseAllEdges = false
FEATURE [PartDesign::Body] Body015  label="lid-side"
  AllowCompound = false
  Group = -> [Sketch027,Pad013,Sketch028,Pocket008,Sketch029,Pocket009,Chamfer006]
  Origin = -> Origin018
  Tip = -> Chamfer006
FEATURE [PartDesign::FeatureBase] Clone007
  BaseFeature = -> Body013
  Placement = pos=(20,0,0) rot=(0,0,1;0rad)
  Suppressed = false
FEATURE [PartDesign::Body] Body016
  AllowCompound = false
  Group = -> [Clone007]
  Origin = -> Origin019
  Placement = pos=(120,0,30) rot=(0,0,1;0rad)
  Tip = -> Clone007
FEATURE [Part::FeaturePython] Slice002  # WARN: FeaturePython — macro-defined, semantics opaque (R4)
  Base = -> Body016
  Mode = 1
  Tolerance = 0
  Tools = -> [Plane]
FEATURE [Part::FeaturePython] Slice002_child0  label="Slice002.0"  # WARN: FeaturePython — macro-defined, semantics opaque (R4)
  Base = -> Slice002
  FilterType = 1
  Invert = false
  OverrideMaxVal = 0
  WindowFrom = 80
  WindowTo = 100
  items = 0
FEATURE [Part::FeaturePython] Slice002_child1  label="Slice002.1"  # WARN: FeaturePython — macro-defined, semantics opaque (R4)
  Base = -> Slice002
  FilterType = 1
  Invert = false
  OverrideMaxVal = 0
  WindowFrom = 80
  WindowTo = 100
  items = 1
FEATURE [App::DocumentObjectGroup] GrExplode_Slice002  label="Exploded Slice002"
  Group = -> [Slice002_child0,Slice002_child1]
FEATURE [PartDesign::FeatureBase] BaseFeature002
  BaseFeature = -> Slice002_child0
  Suppressed = false
FEATURE [PartDesign::FeatureBase] BaseFeature003
  BaseFeature = -> Slice002_child1
  Suppressed = false
FEATURE [Sketcher::SketchObject] Sketch030
  ArcFitTolerance = 1e-06
  AttachmentSupport = -> [BaseFeature002]
  ExternalGeometry = -> [BaseFeature002]
  FullyConstrained = true
  MakeInternals = false
  MapMode = 5
  Placement = pos=(0,0,30) rot=(1,0,0;3.14159rad)
  sketch-geometry (2):
    g0: Circle CenterX=187 CenterY=-78 CenterZ=0 NormalX=0 NormalY=0 NormalZ=1 AngleXU=0 Radius=1.3
    g1: Circle CenterX=187 CenterY=-12 CenterZ=0 NormalX=0 NormalY=0 NormalZ=1 AngleXU=0 Radius=1.3
  constraints (6):
    c: Diameter(g0) = 2.6
    c: DistanceX(g0,g-5) = 8
    c: DistanceY(g-5,g0) = 12
    c: Diameter(g1) = 2.6
    c: DistanceX(g1,g-4) = 8
    c: DistanceY(g1,g-4) = 12
FEATURE [Sketcher::SketchObject] Sketch031
  ArcFitTolerance = 1e-06
  AttachmentSupport = -> [BaseFeature003]
  ExternalGeometry = -> [BaseFeature003]
  FullyConstrained = true
  MakeInternals = false
  MapMode = 5
  Placement = pos=(0,0,30) rot=(1,0,0;3.14159rad)
  sketch-geometry (2):
    g0: Circle CenterX=203 CenterY=-78 CenterZ=0 NormalX=0 NormalY=0 NormalZ=1 AngleXU=0 Radius=1.3
    g1: Circle CenterX=203 CenterY=-12 CenterZ=0 NormalX=0 NormalY=0 NormalZ=1 AngleXU=0 Radius=1.3
  constraints (6):
    c: Diameter(g0) = 2.6
    c: DistanceX(g-4,g0) = 8
    c: DistanceY(g-4,g0) = 12
    c: Diameter(g1) = 2.6
    c: DistanceY(g1,g-3) = 12
    c: DistanceX(g-3,g1) = 8
FEATURE [PartDesign::Pocket] Pocket010
  BaseFeature = -> BaseFeature003
  Direction = (0,0,1)
  Length = 7
  Length2 = 5
  Profile = -> Sketch031
  ReferenceAxis = -> Sketch031 [N_Axis]
  Refine = true
  Suppressed = false
  Type = 0
FEATURE [PartDesign::Body] Body018  label="right-lid-split"
  AllowCompound = false
  BaseFeature = -> Slice002_child1
  Group = -> [BaseFeature003,Sketch031,Pocket010]
  Origin = -> Origin021
  Placement = pos=(0,0,-30) rot=(0,0,1;0rad)
  Tip = -> Pocket010
FEATURE [PartDesign::Pocket] Pocket011
  BaseFeature = -> BaseFeature002
  Direction = (0,0,1)
  Length = 7
  Length2 = 5
  Profile = -> Sketch030
  ReferenceAxis = -> Sketch030 [N_Axis]
  Refine = true
  Suppressed = false
  Type = 0
FEATURE [PartDesign::Body] Body017  label="left-lid-split"
  AllowCompound = false
  BaseFeature = -> Slice002_child0
  Group = -> [BaseFeature002,Sketch030,Pocket011]
  Origin = -> Origin020
  Placement = pos=(20,0,-30) rot=(0,0,1;0rad)
  Tip = -> Pocket011
FEATURE [PartDesign::FeatureBase] Clone008
  BaseFeature = -> Body013
  Placement = pos=(20,0,0) rot=(0,0,1;0rad)
  Suppressed = false
FEATURE [PartDesign::Body] Body019  label="lid-module-clone001"
  AllowCompound = false
  Group = -> [Clone008]
  Origin = -> Origin023
  Placement = pos=(190,0,0) rot=(0,0,1;0rad)
  Tip = -> Clone008
FEATURE [PartDesign::FeatureBase] Clone009
  BaseFeature = -> Body013
  Placement = pos=(20,0,0) rot=(0,0,1;0rad)
  Suppressed = false
FEATURE [PartDesign::Body] Body020  label="lid-module-clone002"
  AllowCompound = false
  Group = -> [Clone009]
  Origin = -> Origin024
  Placement = pos=(260,0,0) rot=(0,0,1;0rad)
  Tip = -> Clone009
FEATURE [Sketcher::SketchObject] Sketch032
  ArcFitTolerance = 1e-06
  AttachmentSupport = -> [XY_Plane025]
  FullyConstrained = true
  MakeInternals = false
  MapMode = 5
  sketch-geometry (4):
    g0: LineSegment StartX=0 StartY=0 StartZ=0 EndX=20 EndY=0 EndZ=0
    g1: LineSegment StartX=20 StartY=0 StartZ=0 EndX=20 EndY=90 EndZ=0
    g2: LineSegment StartX=20 StartY=90 StartZ=0 EndX=0 EndY=90 EndZ=0
    g3: LineSegment StartX=0 StartY=90 StartZ=0 EndX=0 EndY=0 EndZ=0
  constraints (11):
    c: Coincident(g0,g1)
    c: Coincident(g1,g2)
    c: Coincident(g2,g3)
    c: Coincident(g3,g0)
    c: Horizontal(g0)
    c: Horizontal(g2)
    c: Vertical(g1)
    c: Vertical(g3)
    c: Distance(g1,g3) = 20
    c: Distance(g0,g2) = 90
    c: Coincident(g0,g-1)
FEATURE [PartDesign::Pad] Pad014
  Direction = (0,0,1)
  Length = 9
  Length2 = 10
  Profile = -> Sketch032
  ReferenceAxis = -> Sketch032 [N_Axis]
  Refine = true
  Suppressed = false
  Type = 0
FEATURE [PartDesign::Chamfer] Chamfer007
  Angle = 45
  Base = -> Pad014 [Edge10,Edge4]
  BaseFeature = -> Pad014
  ChamferType = 0
  FlipDirection = false
  Refine = true
  Size = 4
  Size2 = 1
  SupportTransform = false
  Suppressed = false
  UseAllEdges = false
FEATURE [Sketcher::SketchObject] Sketch033
  ArcFitTolerance = 1e-06
  AttachmentSupport = -> [Chamfer007]
  ExternalGeometry = -> [Chamfer007]
  FullyConstrained = true
  MakeInternals = false
  MapMode = 5
  Placement = pos=(0,0,9) rot=(0,0,1;0rad)
  sketch-geometry (2):
    g0: Circle CenterX=10 CenterY=61 CenterZ=0 NormalX=0 NormalY=0 NormalZ=1 AngleXU=0 Radius=4
    g1: Circle CenterX=10 CenterY=29 CenterZ=0 NormalX=0 NormalY=0 NormalZ=1 AngleXU=0 Radius=3.125
  constraints (6):
    c: Diameter(g0) = 8
    c: Diameter(g1) = 6.25
    c: DistanceX(g-3,g0) = 10
    c: DistanceX(g-4,g1) = 10
    c: DistanceY(g-4,g1) = 25
    c: DistanceY(g0,g-3) = 25
FEATURE [PartDesign::Pocket] Pocket012
  BaseFeature = -> Chamfer007
  Direction = (0,0,-1)
  Length = 10
  Length2 = 5
  Profile = -> Sketch033
  ReferenceAxis = -> Sketch033 [N_Axis]
  Refine = true
  Suppressed = false
  Type = 0
FEATURE [Sketcher::SketchObject] Sketch034
  ArcFitTolerance = 1e-06
  AttachmentSupport = -> [Pocket012]
  FullyConstrained = true
  MakeInternals = false
  MapMode = 5
  Placement = pos=(0,0,0) rot=(1,0,0;3.14159rad)
  sketch-geometry (4):
    g0: LineSegment StartX=3 StartY=-22 StartZ=0 EndX=3 EndY=-36 EndZ=0
    g1: LineSegment StartX=3 StartY=-36 StartZ=0 EndX=17 EndY=-36 EndZ=0
    g2: LineSegment StartX=17 StartY=-36 StartZ=0 EndX=17 EndY=-22 EndZ=0
    g3: LineSegment StartX=17 StartY=-22 StartZ=0 EndX=3 EndY=-22 EndZ=0
  constraints (12):
    c: Coincident(g0,g1)
    c: Coincident(g1,g2)
    c: Coincident(g2,g3)
    c: Coincident(g3,g0)
    c: Vertical(g0)
    c: Vertical(g2)
    c: Horizontal(g1)
    c: Horizontal(g3)
    c: Distance(g0,g2) = 14
    c: Distance(g1,g3) = 14
    c: DistanceX(g-1,g0) = 3
    c: DistanceY(g0,g-1) = 22
FEATURE [PartDesign::Pocket] Pocket013
  BaseFeature = -> Pocket012
  Direction = (0,0,1)
  Length = 5
  Length2 = 5
  Profile = -> Sketch034
  ReferenceAxis = -> Sketch034 [N_Axis]
  Refine = true
  Suppressed = false
  Type = 0
FEATURE [PartDesign::Body] Body021  label="mode-selector-section"
  AllowCompound = false
  Group = -> [Sketch032,Pad014,Chamfer007,Sketch033,Pocket012,Sketch034,Pocket013]
  Origin = -> Origin025
  Placement = pos=(350,0,0) rot=(0,0,1;0rad)
  Tip = -> Pocket013
FEATURE [PartDesign::FeatureBase] Clone010
  BaseFeature = -> Body015
  Suppressed = false
FEATURE [PartDesign::Body] Body022  label="lid-side-clone"
  AllowCompound = false
  Group = -> [Clone010]
  Origin = -> Origin026
  Placement = pos=(390,90,0) rot=(0,0,1;3.14159rad)
  Tip = -> Clone010
FEATURE [Part::Part2DObjectPython] ShapeString  # Draft 2D object (typed FeaturePython)
  FontFile = <path>
  Fuse = false
  Justification = 4
  JustificationReference = 0
  KeepLeftMargin = false
  MakeFace = true
  ObliqueAngle = 0
  Placement = pos=(55,48,9) rot=(0,0,1;0rad)
  ScaleToSize = true
  Size = 35
  String = A
  Tracking = 0
FEATURE [Part::Extrusion] Extrude
  Base = -> ShapeString
  Dir = (0,0,1)
  DirMode = 2
  FaceMakerClass = Part::FaceMakerBullseye
  FaceMakerMode = 3
  LengthFwd = 1
  LengthRev = 0
  Placement = pos=(0,0,-1) rot=(0,0,1;0rad)
  Solid = false
  Symmetric = false
FEATURE [Part::Cut] Cut
  Base = -> Body013
  Tool = -> Extrude
FEATURE [Part::Part2DObjectPython] ShapeString001  # Draft 2D object (typed FeaturePython)
  FontFile = <path>
  Fuse = false
  Justification = 4
  JustificationReference = 0
  KeepLeftMargin = false
  MakeFace = true
  ObliqueAngle = 0
  ScaleToSize = true
  Size = 35
  String = B
  Tracking = 0
FEATURE [Part::Extrusion] Extrude001
  Base = -> ShapeString001
  Dir = (0,0,1)
  DirMode = 2
  FaceMakerClass = Part::FaceMakerBullseye
  FaceMakerMode = 3
  LengthFwd = 1
  LengthRev = 0
  Placement = pos=(125,48,8) rot=(0,0,1;0rad)
  Solid = false
  Symmetric = false
FEATURE [Part::Cut] Cut001
  Base = -> Body014
  Tool = -> Extrude001
FEATURE [Part::Part2DObjectPython] ShapeString002  # Draft 2D object (typed FeaturePython)
  FontFile = <path>
  Fuse = false
  Justification = 4
  JustificationReference = 0
  KeepLeftMargin = false
  MakeFace = true
  ObliqueAngle = 0
  ScaleToSize = true
  Size = 35
  String = C
  Tracking = 0
FEATURE [Part::Extrusion] Extrude002
  Base = -> ShapeString002
  Dir = (0,0,1)
  DirMode = 2
  FaceMakerClass = Part::FaceMakerBullseye
  FaceMakerMode = 3
  LengthFwd = 1
  LengthRev = 0
  Placement = pos=(195,48,8) rot=(0,0,1;0rad)
  Solid = false
  Symmetric = false
FEATURE [Part::Cut] Cut002
  Base = -> Body017
  Tool = -> Extrude002
FEATURE [App::Part] Part002  label="left-lid"
  Group = -> [Body015,ShapeString,Body013,Extrude,Cut,Body014,Extrude001,ShapeString001,Cut001,Plane,Body002,Body017,Body016,Slice002_child1,Slice002,Slice,Slice002_child0,Extrude002,ShapeString002,Cut002]
  Origin = -> Origin015
  Placement = pos=(-20,120,0) rot=(0,0,1;0rad)
FEATURE [Part::Part2DObjectPython] ShapeString003  # Draft 2D object (typed FeaturePython)
  FontFile = <path>
  Fuse = false
  Justification = 4
  JustificationReference = 0
  KeepLeftMargin = false
  MakeFace = true
  ObliqueAngle = 0
  ScaleToSize = true
  Size = 35
  String = D
  Tracking = 0
FEATURE [Part::Extrusion] Extrude003
  Base = -> ShapeString003
  Dir = (0,0,1)
  DirMode = 2
  FaceMakerClass = Part::FaceMakerBullseye
  FaceMakerMode = 3
  LengthFwd = 1
  LengthRev = 0
  Placement = pos=(245,48,8) rot=(0,0,1;0rad)
  Solid = false
  Symmetric = false
FEATURE [Part::Cut] Cut003
  Base = -> Body019
  Tool = -> Extrude003
FEATURE [Part::Part2DObjectPython] ShapeString004  # Draft 2D object (typed FeaturePython)
  FontFile = <path>
  Fuse = false
  Justification = 4
  JustificationReference = 0
  KeepLeftMargin = false
  MakeFace = true
  ObliqueAngle = 0
  ScaleToSize = true
  Size = 35
  String = E
  Tracking = 0
FEATURE [Part::Extrusion] Extrude004
  Base = -> ShapeString004
  Dir = (0,0,1)
  DirMode = 2
  FaceMakerClass = Part::FaceMakerBullseye
  FaceMakerMode = 3
  LengthFwd = 1
  LengthRev = 0
  Placement = pos=(315,48,8) rot=(0,0,1;0rad)
  Solid = false
  Symmetric = false
FEATURE [Part::Cut] Cut004
  Base = -> Body020
  Tool = -> Extrude004
FEATURE [App::Part] Part003  label="right-lid"
  Group = -> [Body018,Body021,Body022,Body019,Extrude003,ShapeString003,Cut003,Body020,Extrude004,ShapeString004,Cut004]
  Origin = -> Origin022
  Placement = pos=(0,120,0) rot=(0,0,1;0rad)
FEATURE [Sketcher::SketchObject] Sketch035
  ArcFitTolerance = 1e-06
  AttachmentSupport = -> [Clone]
  ExternalGeometry = -> [Clone]
  FullyConstrained = true
  MakeInternals = false
  MapMode = 5
  Placement = pos=(0,90,0) rot=(0,0.707107,0.707107;3.14159rad)
  sketch-geometry (4):
    g0: Circle CenterX=-40 CenterY=17 CenterZ=0 NormalX=0 NormalY=0 NormalZ=1 AngleXU=0 Radius=8
    g1: Circle CenterX=-29 CenterY=17 CenterZ=0 NormalX=0 NormalY=0 NormalZ=1 AngleXU=0 Radius=1.3
    g2: Circle CenterX=-51 CenterY=17 CenterZ=0 NormalX=0 NormalY=0 NormalZ=1 AngleXU=0 Radius=1.3
    g3: Circle CenterX=-10 CenterY=17 CenterZ=0 NormalX=0 NormalY=0 NormalZ=1 AngleXU=0 Radius=6
  constraints (12):
    c: Diameter(g0) = 16
    c: DistanceY(g0,g-4) = 13
    c: DistanceX(g-4,g0) = 30
    c: Diameter(g1) = 2.6
    c: Diameter(g2) = 2.6
    c: DistanceY(g0,g1) = 0
    c: DistanceY(g0,g2) = 0
    c: DistanceX(g2,g0) = 11
    c: DistanceX(g0,g1) = 11
    c: Diameter(g3) = 12
    c: DistanceY(g3,g-4) = 13
    c: DistanceX(g3,g-4) = 10
FEATURE [PartDesign::Pocket] Pocket014
  BaseFeature = -> Clone
  Direction = (0,-1,2e-16)
  Length = 7
  Length2 = 5
  Profile = -> Sketch035
  ReferenceAxis = -> Sketch035 [N_Axis]
  Refine = true
  Suppressed = false
  Type = 0
FEATURE [Sketcher::SketchObject] Sketch036
  ArcFitTolerance = 1e-06
  AttachmentSupport = -> [Pocket014]
  ExternalGeometry = -> [Pocket014]
  FullyConstrained = true
  MakeInternals = false
  MapMode = 5
  Placement = pos=(0,83,0) rot=(1,0,0;1.5708rad)
  sketch-geometry (1):
    g0: Circle CenterX=10 CenterY=17 CenterZ=0 NormalX=0 NormalY=0 NormalZ=1 AngleXU=0 Radius=8.5
  constraints (3):
    c: Diameter(g0) = 17
    c: DistanceY(g0,g-3) = 13
    c: DistanceX(g-3,g0) = 10
FEATURE [PartDesign::Pocket] Pocket015
  BaseFeature = -> Pocket014
  Direction = (0,1,-2e-16)
  Length = 3
  Length2 = 5
  Profile = -> Sketch036
  ReferenceAxis = -> Sketch036 [N_Axis]
  Refine = true
  Suppressed = false
  Type = 0
FEATURE [PartDesign::Body] Body001  label="io-base-module"
  AllowCompound = false
  Group = -> [Clone,Sketch035,Pocket014,Sketch036,Pocket015]
  Origin = -> Origin001
  Tip = -> Pocket015
FEATURE [Sketcher::SketchObject] Sketch037
  ArcFitTolerance = 1e-06
  AttachmentSupport = -> [XY_Plane030]
  FullyConstrained = true
  MakeInternals = false
  MapMode = 5
  sketch-geometry (1):
    g0: Circle CenterX=0 CenterY=0 CenterZ=0 NormalX=0 NormalY=0 NormalZ=1 AngleXU=0 Radius=4
  constraints (2):
    c: Diameter(g0) = 8
    c: Coincident(g0,g-1)
FEATURE [PartDesign::Plane] DatumPlane
  AttachmentOffset = pos=(0,0,4) rot=(0,0,1;0rad)
  AttachmentSupport = -> [Sketch037]
  Length = 60
  MapMode = 2
  Placement = pos=(0,0,4) rot=(0,0,1;0rad)
  ResizeMode = 0
  Width = 60
FEATURE [Sketcher::SketchObject] Sketch038
  ArcFitTolerance = 1e-06
  AttachmentSupport = -> [DatumPlane]
  FullyConstrained = true
  MakeInternals = false
  MapMode = 5
  Placement = pos=(0,0,4) rot=(0,0,1;0rad)
  sketch-geometry (1):
    g0: Circle CenterX=0 CenterY=0 CenterZ=0 NormalX=0 NormalY=0 NormalZ=1 AngleXU=0 Radius=1.25
  constraints (2):
    c: Diameter(g0) = 2.5
    c: Coincident(g0,g-1)
FEATURE [PartDesign::AdditiveLoft] AdditiveLoft
  Closed = false
  Placement = pos=(0,0,4) rot=(0,0,1;0rad)
  Profile = -> Sketch038
  Refine = true
  Ruled = false
  Sections = -> [Sketch037]
  Suppressed = false
FEATURE [Sketcher::SketchObject] Sketch039
  ArcFitTolerance = 1e-06
  AttachmentSupport = -> [AdditiveLoft]
  FullyConstrained = true
  MakeInternals = false
  MapMode = 5
  Placement = pos=(0,0,4) rot=(0,0,1;0rad)
  sketch-geometry (1):
    g0: Circle CenterX=0 CenterY=0 CenterZ=0 NormalX=0 NormalY=0 NormalZ=1 AngleXU=0 Radius=0.85
  constraints (2):
    c: Diameter(g0) = 1.7
    c: Coincident(g0,g-1)
FEATURE [PartDesign::Pocket] Pocket016
  BaseFeature = -> AdditiveLoft
  Direction = (0,0,-1)
  Length = 5
  Length2 = 5
  Placement = pos=(0,0,4) rot=(0,0,1;0rad)
  Profile = -> Sketch039
  ReferenceAxis = -> Sketch039 [N_Axis]
  Refine = true
  Suppressed = false
  Type = 0
FEATURE [PartDesign::Body] Body023  label="standoff"
  AllowCompound = false
  Group = -> [Sketch037,DatumPlane,Sketch038,AdditiveLoft,Sketch039,Pocket016]
  Origin = -> Origin030
  Tip = -> Pocket016
FEATURE [App::Link] standoff004  label="standoff005"
  LinkedObject = -> Body023
FEATURE [App::FeaturePython] GroundedJoint  # Assembly grounded joint (typed FeaturePython)
  ObjectToGround = -> standoff004
FEATURE [Assembly::JointGroup] Joints001
  Group = -> [GroundedJoint]
FEATURE [App::Link] standoff005  label="standoff006"
  LinkPlacement = pos=(64.8,0,0) rot=(0,0,1;0rad)
  LinkedObject = -> Body023
  Placement = pos=(64.8,0,0) rot=(0,0,1;0rad)
FEATURE [App::Link] standoff006  label="standoff007"
  LinkPlacement = pos=(0,45,0) rot=(0,0,1;0rad)
  LinkedObject = -> Body023
  Placement = pos=(0,45,0) rot=(0,0,1;0rad)
FEATURE [App::Link] standoff007  label="standoff008"
  LinkPlacement = pos=(64.8,45,0) rot=(0,0,1;0rad)
  LinkedObject = -> Body023
  Placement = pos=(64.8,45,0) rot=(0,0,1;0rad)
FEATURE [Assembly::AssemblyObject] Assembly001  label="standoffs001"
  Group = -> [Joints001,standoff004,GroundedJoint,standoff005,standoff006,standoff007]
  Origin = -> Origin029
  Placement = pos=(77,35,7) rot=(0,0,1;0rad)
  Type = Assembly
FEATURE [App::Part] Part  label="left-base"
  Group = -> [Body005,Body001,Body,Body011,Assembly001]
  Origin = -> Origin011
note: 5 file-system paths scrubbed to <path> (originals preserved in the JSON sidecar)
